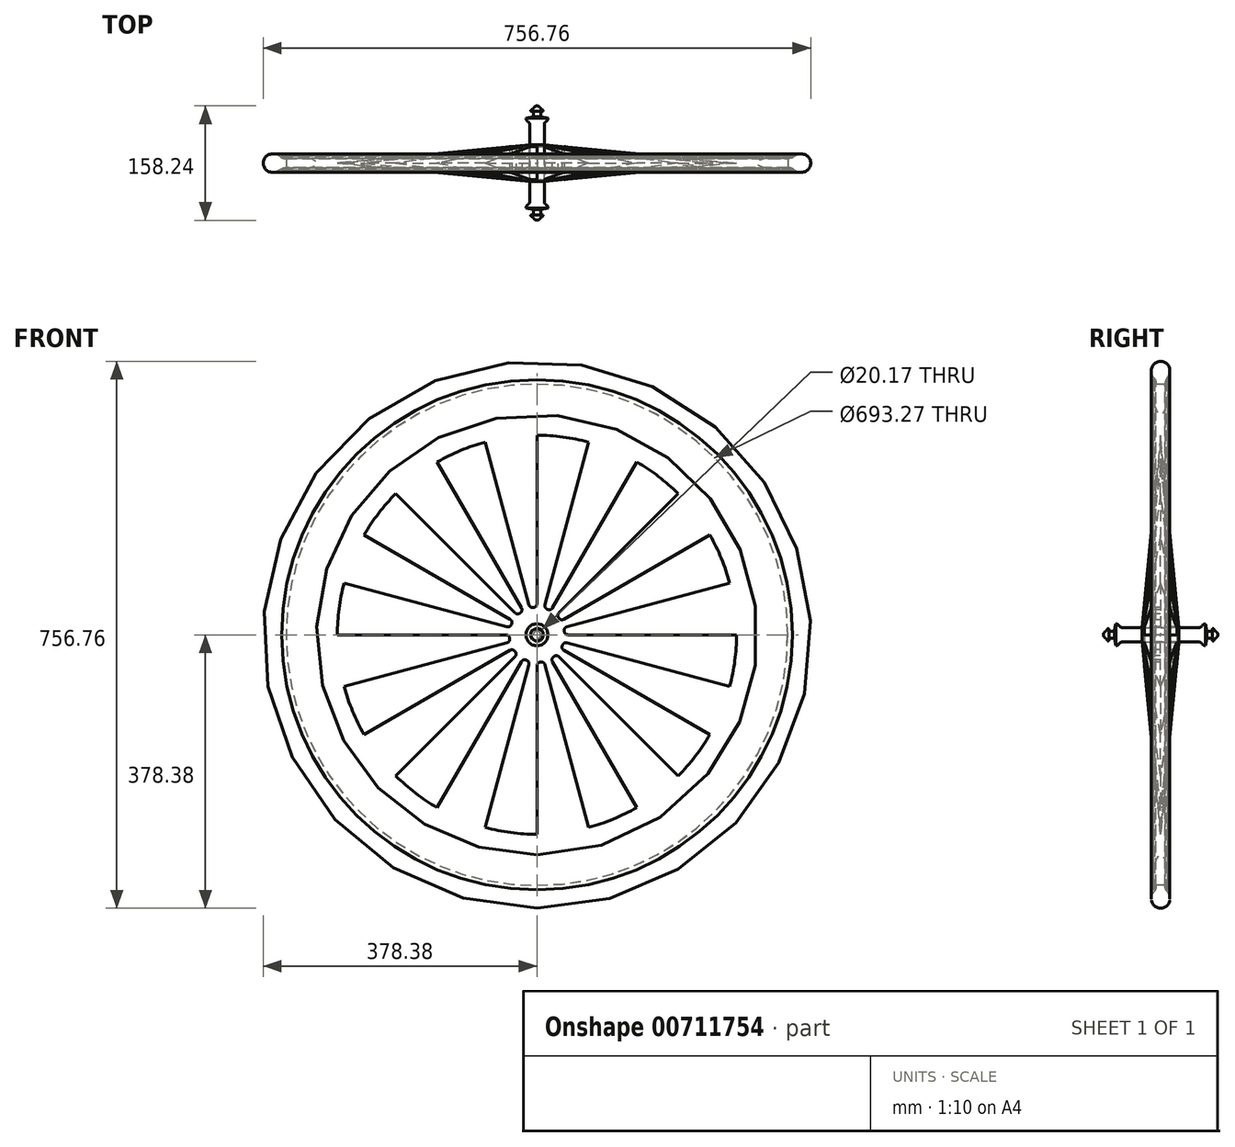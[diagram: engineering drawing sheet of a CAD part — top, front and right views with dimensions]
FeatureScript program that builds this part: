
annotation { "Feature Type Name" : "Feature", "Feature Type Description" : "" }
export const myFeature = defineFeature(function(context is Context, id is Id, definition is map)
    precondition{}
    {
        {
            var Q0;
            Q0=qCreatedBy(makeId("Right.planeOp"),FACE);
            var sketch = newSketch(context, id + "F0", { "sketchPlane" : qUnion([Q0])});
            skLineSegment(sketch, "E0.bottom", {"start": v(71.5, 5) * mm, "end": v(63.88, 5) * mm});
            skPoint(sketch, "E0.middle", {"position": v(0, 0) * mm});
            skLineSegment(sketch, "E1", {"start": v(0, 0) * mm, "end": v(0, 51.2) * mm, "construction": true});
            skLineSegment(sketch, "E2", {"start": v(71.5, 5) * mm, "end": v(71.5, 7.54) * mm});
            skLineSegment(sketch, "E3", {"start": v(71.5, 15) * mm, "end": v(71.5, 19.5) * mm, "construction": true});
            skArc(sketch, "E4", {"start": v(73.4, 8.06) * mm, "mid": v(75.04, 5.82) * mm, "end": v(77.1, 3.96) * mm});
            skArc(sketch, "E5", {"start": v(77.1, 3.96) * mm, "mid": v(78.59, 2.22) * mm, "end": v(79.12, 0) * mm});
            skPoint(sketch, "E6.visualSharp", {"position": v(71.5, 15) * mm});
            skArc(sketch, "E6.filletArc", {"start": v(73.4, 8.06) * mm, "mid": v(72.25, 8.52) * mm, "end": v(71.5, 7.54) * mm});
            skLineSegment(sketch, "E7.MirrorCS", {"start": v(62.09, 15.16) * mm, "end": v(139.74, 15.16) * mm, "construction": true});
            skLineSegment(sketch, "E8.MirrorCS", {"start": v(62.09, 15.16) * mm, "end": v(63.88, 5) * mm});
            skArc(sketch, "E9.MirrorCS", {"start": v(62.09, 15.16) * mm, "mid": v(59.32, 14.42) * mm, "end": v(57.3, 12.38) * mm});
            skArc(sketch, "E10.MirrorCS", {"start": v(53.34, 10.08) * mm, "mid": v(55.62, 10.7) * mm, "end": v(57.3, 12.38) * mm});
            skLineSegment(sketch, "E11.MirrorCS", {"start": v(53.34, 10.08) * mm, "end": v(0, 10.08) * mm});
            skLineSegment(sketch, "E12", {"start": v(0, 0) * mm, "end": v(79.12, 0) * mm});
            skLineSegment(sketch, "E13.MirrorCS", {"start": v(-71.5, 5) * mm, "end": v(-71.5, 7.54) * mm});
            skPoint(sketch, "E14.MirrorP", {"position": v(-71.5, 15) * mm});
            skLineSegment(sketch, "E15.MirrorCS", {"start": v(-71.5, 5) * mm, "end": v(-63.88, 5) * mm});
            skLineSegment(sketch, "E16.MirrorCS", {"start": v(0, 0) * mm, "end": v(-79.12, 0) * mm});
            skArc(sketch, "E17.MirrorCS", {"start": v(-73.4, 8.06) * mm, "mid": v(-75.04, 5.82) * mm, "end": v(-77.1, 3.96) * mm});
            skLineSegment(sketch, "E18.MirrorCS", {"start": v(-71.5, 15) * mm, "end": v(-71.5, 19.5) * mm, "construction": true});
            skLineSegment(sketch, "E19.MirrorCS", {"start": v(-53.34, 10.08) * mm, "end": v(0, 10.08) * mm});
            skLineSegment(sketch, "E20.MirrorCS", {"start": v(-62.09, 15.16) * mm, "end": v(-139.74, 15.16) * mm, "construction": true});
            skArc(sketch, "E21.MirrorCS", {"start": v(-53.34, 10.08) * mm, "mid": v(-55.62, 10.7) * mm, "end": v(-57.3, 12.38) * mm});
            skArc(sketch, "E22.MirrorCS", {"start": v(-62.09, 15.16) * mm, "mid": v(-59.32, 14.42) * mm, "end": v(-57.3, 12.38) * mm});
            skLineSegment(sketch, "E23.MirrorCS", {"start": v(-62.09, 15.16) * mm, "end": v(-63.88, 5) * mm});
            skArc(sketch, "E24.MirrorCS", {"start": v(-73.4, 8.06) * mm, "mid": v(-72.25, 8.52) * mm, "end": v(-71.5, 7.54) * mm});
            skArc(sketch, "E25.MirrorCS", {"start": v(-77.1, 3.96) * mm, "mid": v(-78.59, 2.22) * mm, "end": v(-79.12, 0) * mm});
            skSolve(sketch);
        }
        {
            var Q0;
            Q0=makeQuery(id+"F0.imprint","IMPRINT",FACE,{"disambiguationData":[TD([[makeQuery(id+"F0.imprint","IMPRINT",EDGE,{"derivedFrom":sQuery(id+"F0.wireOp",EDGE,"E0.bottom")}),1.0]])]});
            var Q1;
            Q1=sQuery(id+"F0.wireOp",EDGE,"E16.MirrorCS");
            revolve(context, id + "F1", {"entities" : qUnion([Q0]), "axis" : qUnion([Q1]), "revolveType" : RevolveType.FULL});
        }
        {
            var Q0;
            Q0=qCreatedBy(makeId("Right.planeOp"),FACE);
            var sketch = newSketch(context, id + "F2", { "sketchPlane" : qUnion([Q0])});
            skLineSegment(sketch, "E26", {"start": v(-53.34, 10.08) * mm, "end": v(53.34, 10.08) * mm, "construction": true});
            skArc(sketch, "E27", {"start": v(-57.3, 12.38) * mm, "mid": v(-59.32, 14.42) * mm, "end": v(-62.09, 15.16) * mm, "construction": true});
            skArc(sketch, "E28", {"start": v(-57.3, 12.38) * mm, "mid": v(-55.62, 10.7) * mm, "end": v(-53.34, 10.08) * mm, "construction": true});
            skArc(sketch, "E29", {"start": v(53.34, 10.08) * mm, "mid": v(55.62, 10.7) * mm, "end": v(57.3, 12.38) * mm, "construction": true});
            skArc(sketch, "E30", {"start": v(62.09, 15.16) * mm, "mid": v(59.32, 14.42) * mm, "end": v(57.3, 12.38) * mm, "construction": true});
            skLineSegment(sketch, "E31", {"start": v(0, 10.08) * mm, "end": v(53.34, 10.08) * mm});
            skLineSegment(sketch, "E32", {"start": v(-31.75, 10.08) * mm, "end": v(26.67, 10.08) * mm});
            skLineSegment(sketch, "E33", {"start": v(-53.34, 10.08) * mm, "end": v(0, 365.68) * mm, "construction": true});
            skLineSegment(sketch, "E34", {"start": v(0, 365.68) * mm, "end": v(53.34, 10.08) * mm, "construction": true});
            skArc(sketch, "E35", {"start": v(-1.88, 353.12) * mm, "mid": v(0, 352.98) * mm, "end": v(1.88, 353.12) * mm, "construction": true});
            skLineSegment(sketch, "E36.top", {"start": v(6.35, 346.63) * mm, "end": v(-6.35, 346.63) * mm});
            skPoint(sketch, "E36.middle", {"position": v(0, 352.98) * mm});
            skPoint(sketch, "E37.orphan", {"position": v(-6.35, 359.33) * mm});
            skPoint(sketch, "E38.orphan", {"position": v(6.35, 359.33) * mm});
            skArc(sketch, "E39.trimOffspring", {"start": v(12.6, 367.23) * mm, "mid": v(0, 378.38) * mm, "end": v(-12.6, 367.23) * mm});
            skPoint(sketch, "E40.visualSharp", {"position": v(-6.35, 354.69) * mm});
            skPoint(sketch, "E41.visualSharp", {"position": v(6.35, 354.69) * mm});
            skArc(sketch, "E42", {"start": v(-12.6, 367.23) * mm, "mid": v(-12.07, 360.76) * mm, "end": v(-9, 355.04) * mm});
            skArc(sketch, "E43", {"start": v(-6.35, 346.63) * mm, "mid": v(-6.85, 351.1) * mm, "end": v(-9, 355.04) * mm});
            skArc(sketch, "E44", {"start": v(9, 355.04) * mm, "mid": v(12.07, 360.76) * mm, "end": v(12.6, 367.23) * mm});
            skArc(sketch, "E45", {"start": v(9, 355.04) * mm, "mid": v(6.85, 351.1) * mm, "end": v(6.35, 346.63) * mm});
            skLineSegment(sketch, "E46", {"start": v(0, 365.68) * mm, "end": v(0, 346.63) * mm, "construction": true});
            skArc(sketch, "E47.0", {"start": v(-6.38, 346.6) * mm, "mid": v(-6.56, 349.87) * mm, "end": v(-7.65, 352.96) * mm});
            skLineSegment(sketch, "E47.1", {"start": v(6.38, 346.6) * mm, "end": v(-6.38, 346.6) * mm});
            skArc(sketch, "E47.2", {"start": v(7.65, 352.96) * mm, "mid": v(6.56, 349.87) * mm, "end": v(6.38, 346.6) * mm});
            skLineSegment(sketch, "E48", {"start": v(-7.65, 352.96) * mm, "end": v(-10.16, 352.96) * mm});
            skLineSegment(sketch, "E49", {"start": v(-10.16, 352.96) * mm, "end": v(-10.16, 342.8) * mm});
            skLineSegment(sketch, "E50", {"start": v(-10.16, 342.8) * mm, "end": v(0, 342.8) * mm});
            skLineSegment(sketch, "E51.MirrorCS", {"start": v(10.16, 352.96) * mm, "end": v(10.16, 342.8) * mm});
            skLineSegment(sketch, "E52.MirrorCS", {"start": v(10.16, 342.8) * mm, "end": v(0, 342.8) * mm});
            skLineSegment(sketch, "E53.MirrorCS", {"start": v(7.65, 352.96) * mm, "end": v(10.16, 352.96) * mm});
            skEllipticalArc(sketch, "E54", {});
            skLineSegment(sketch, "E55", {"start": v(0, 342.8) * mm, "end": v(-31.75, 10.08) * mm});
            skLineSegment(sketch, "E56.MirrorCS", {"start": v(0, 342.8) * mm, "end": v(31.75, 10.08) * mm});
            skLineSegment(sketch, "E57.0", {"start": v(0, 275.95) * mm, "end": v(-25.43, 9.48) * mm});
            skLineSegment(sketch, "E57.1", {"start": v(0, 275.95) * mm, "end": v(25.43, 9.48) * mm});
            const initialGuessF2  = {"E54": [0, 0.34279840000000006, 1, 0, 0.01016, 0.0381, 3.141592653589793, 6.283185307179586]};
            skSetInitialGuess(sketch, initialGuessF2);
            skSolve(sketch);
        }
        {
            var Q0;
            Q0=makeQuery(id+"F2.imprint","IMPRINT",FACE,{"disambiguationData":[TD([[makeQuery(id+"F2.imprint","IMPRINT",EDGE,{"derivedFrom":sQuery(id+"F2.wireOp",EDGE,"E36.top")}),-1.0]])]});
            var Q1;
            Q1=makeQuery(id+"F2.imprint","IMPRINT",FACE,{"disambiguationData":[TD([[makeQuery(id+"F2.imprint","IMPRINT",EDGE,{"derivedFrom":sQuery(id+"F2.wireOp",EDGE,"E47.0")}),1.0]])]});
            var Q2;
            {var subQ0=sQuery(id+"F2.wireOp",EDGE,"E50");Q2=makeQuery(id+"F2.imprint","IMPRINT",FACE,{"disambiguationData":[TD([[makeQuery(id+"F2.imprint","IMPRINT",EDGE,{"derivedFrom":subQ0}),-1.0]])]});}
            var Q3;
            {var subQ0=sQuery(id+"F2.wireOp",EDGE,"E52.MirrorCS");Q3=makeQuery(id+"F2.imprint","IMPRINT",FACE,{"disambiguationData":[TD([[makeQuery(id+"F2.imprint","IMPRINT",EDGE,{"derivedFrom":subQ0}),1.0]])]});}
            var Q4;
            {var subQ5=sQuery(id+"F2.wireOp",EDGE,"E32");var subQ7=sQuery(id+"F2.wireOp",EDGE,"E31");var subQ8=makeQuery(id+"F2.imprint","INTERSECT",VERTEX,{"derivedFrom":[subQ7,subQ5]});Q4=makeQuery(id+"F2.imprint","IMPRINT",FACE,{"disambiguationData":[TD([[makeQuery(id+"F2.imprint","IMPRINT",EDGE,{"disambiguationData":[TD([[subQ8,-1.0]])],"derivedFrom":subQ7}),1.0]])]});}
            var Q5;
            {var subQ0=sQuery(id+"F2.wireOp",EDGE,"E55");var subQ1=sQuery(id+"F2.wireOp",EDGE,"E54");var subQ2=makeQuery(id+"F2.imprint","INTERSECT",VERTEX,{"derivedFrom":[subQ1,subQ0]});Q5=makeQuery(id+"F2.imprint","IMPRINT",FACE,{"disambiguationData":[TD([[makeQuery(id+"F2.imprint","IMPRINT",EDGE,{"disambiguationData":[TD([[subQ2,-1.0]])],"derivedFrom":subQ1}),1.0]])]});}
            var Q6;
            Q6=makeQuery(id+"F1.opRevolve","SWEPT_FACE",FACE,{"disambiguationData":[OSD([sQuery(id+"F0.wireOp",EDGE,"E11.MirrorCS"),sQuery(id+"F0.wireOp",EDGE,"E19.MirrorCS")])]});
            revolve(context, id + "F3", {"entities" : qUnion([Q0, Q1, Q2, Q3, Q4, Q5]), "axis" : qUnion([Q6]), "revolveType" : RevolveType.FULL});
        }
        {
            var Q0;
            Q0=qCreatedBy(makeId("Front.planeOp"),FACE);
            var sketch = newSketch(context, id + "F4", { "sketchPlane" : qUnion([Q0])});
            skPoint(sketch, "E58.0", {"position": v(0, 0) * mm});
            skLineSegment(sketch, "E59", {"start": v(0, 42.88) * mm, "end": v(0, 279.11) * mm});
            skLineSegment(sketch, "E60", {"start": v(-11.1, 41.42) * mm, "end": v(-72.24, 269.6) * mm});
            skArc(sketch, "E61", {"start": v(-13.28, 291.8) * mm, "mid": v(-38.13, 289.6) * mm, "end": v(-62.7, 285.3) * mm});
            skArc(sketch, "E62", {"start": v(-4.48, 37.84) * mm, "mid": v(-4.97, 37.77) * mm, "end": v(-5.46, 37.7) * mm});
            skPoint(sketch, "E63.visualSharp", {"position": v(0, 292.1) * mm});
            skArc(sketch, "E63.filletArc", {"start": v(0, 279.11) * mm, "mid": v(-3.93, 288.3) * mm, "end": v(-13.28, 291.8) * mm});
            skPoint(sketch, "E64.visualSharp", {"position": v(-75.6, 282.15) * mm});
            skArc(sketch, "E64.filletArc", {"start": v(-62.7, 285.3) * mm, "mid": v(-70.82, 279.49) * mm, "end": v(-72.24, 269.6) * mm});
            skPoint(sketch, "E65.visualSharp", {"position": v(-9.86, 36.8) * mm});
            skArc(sketch, "E65.filletArc", {"start": v(-11.1, 41.42) * mm, "mid": v(-8.99, 38.5) * mm, "end": v(-5.46, 37.7) * mm});
            skPoint(sketch, "E66.visualSharp", {"position": v(0, 38.1) * mm});
            skArc(sketch, "E66.filletArc", {"start": v(-4.48, 37.84) * mm, "mid": v(-1.28, 39.5) * mm, "end": v(0, 42.88) * mm});
            skLineSegment(sketch, "E67", {"start": v(0, 0) * mm, "end": v(0, 306.93) * mm, "construction": true});
            skLineSegment(sketch, "E68.1.0", {"start": v(0, 0) * mm, "end": v(-153.46, 265.8) * mm, "construction": true});
            skLineSegment(sketch, "E68.1.1", {"start": v(-30.32, 30.32) * mm, "end": v(-197.36, 197.36) * mm});
            skPoint(sketch, "E68.1.2", {"position": v(-19.05, 33) * mm});
            skPoint(sketch, "E68.1.3", {"position": v(-26.94, 26.94) * mm});
            skLineSegment(sketch, "E68.1.4", {"start": v(-21.44, 37.14) * mm, "end": v(-139.56, 241.72) * mm});
            skArc(sketch, "E68.1.5", {"start": v(-22.8, 30.53) * mm, "mid": v(-20.86, 33.57) * mm, "end": v(-21.44, 37.14) * mm});
            skArc(sketch, "E68.1.6", {"start": v(-30.32, 30.32) * mm, "mid": v(-27.03, 28.84) * mm, "end": v(-23.58, 29.92) * mm});
            skArc(sketch, "E68.1.7", {"start": v(-22.8, 30.53) * mm, "mid": v(-23.2, 30.23) * mm, "end": v(-23.58, 29.92) * mm});
            skArc(sketch, "E68.1.8", {"start": v(-196.94, 215.72) * mm, "mid": v(-201.08, 206.63) * mm, "end": v(-197.36, 197.36) * mm});
            skArc(sketch, "E68.1.9", {"start": v(-157.4, 246.07) * mm, "mid": v(-177.82, 231.74) * mm, "end": v(-196.94, 215.72) * mm});
            skArc(sketch, "E68.1.10", {"start": v(-139.56, 241.72) * mm, "mid": v(-147.55, 247.7) * mm, "end": v(-157.4, 246.07) * mm});
            skLineSegment(sketch, "E68.2.0", {"start": v(0, 0) * mm, "end": v(-265.8, 153.46) * mm, "construction": true});
            skLineSegment(sketch, "E68.2.1", {"start": v(-41.42, 11.1) * mm, "end": v(-269.6, 72.24) * mm});
            skPoint(sketch, "E68.2.2", {"position": v(-33, 19.05) * mm});
            skPoint(sketch, "E68.2.3", {"position": v(-36.8, 9.86) * mm});
            skLineSegment(sketch, "E68.2.4", {"start": v(-37.14, 21.44) * mm, "end": v(-241.72, 139.56) * mm});
            skArc(sketch, "E68.2.5", {"start": v(-35, 15.04) * mm, "mid": v(-34.85, 18.64) * mm, "end": v(-37.14, 21.44) * mm});
            skArc(sketch, "E68.2.6", {"start": v(-41.42, 11.1) * mm, "mid": v(-37.83, 11.46) * mm, "end": v(-35.39, 14.12) * mm});
            skArc(sketch, "E68.2.7", {"start": v(-35, 15.04) * mm, "mid": v(-35.2, 14.58) * mm, "end": v(-35.39, 14.12) * mm});
            skArc(sketch, "E68.2.8", {"start": v(-278.42, 88.35) * mm, "mid": v(-277.45, 78.4) * mm, "end": v(-269.6, 72.24) * mm});
            skArc(sketch, "E68.2.9", {"start": v(-259.34, 134.4) * mm, "mid": v(-269.87, 111.78) * mm, "end": v(-278.42, 88.35) * mm});
            skArc(sketch, "E68.2.10", {"start": v(-241.72, 139.56) * mm, "mid": v(-251.63, 140.75) * mm, "end": v(-259.34, 134.4) * mm});
            skLineSegment(sketch, "E68.3.0", {"start": v(0, 0) * mm, "end": v(-306.93, 0) * mm, "construction": true});
            skLineSegment(sketch, "E68.3.1", {"start": v(-41.42, -11.1) * mm, "end": v(-269.6, -72.24) * mm});
            skPoint(sketch, "E68.3.2", {"position": v(-38.1, 0) * mm});
            skPoint(sketch, "E68.3.3", {"position": v(-36.8, -9.86) * mm});
            skLineSegment(sketch, "E68.3.4", {"start": v(-42.88, 0) * mm, "end": v(-279.11, 0) * mm});
            skArc(sketch, "E68.3.5", {"start": v(-37.84, -4.48) * mm, "mid": v(-39.5, -1.28) * mm, "end": v(-42.88, 0) * mm});
            skArc(sketch, "E68.3.6", {"start": v(-41.42, -11.1) * mm, "mid": v(-38.5, -8.99) * mm, "end": v(-37.7, -5.46) * mm});
            skArc(sketch, "E68.3.7", {"start": v(-37.84, -4.48) * mm, "mid": v(-37.77, -4.97) * mm, "end": v(-37.7, -5.46) * mm});
            skArc(sketch, "E68.3.8", {"start": v(-285.3, -62.7) * mm, "mid": v(-279.49, -70.82) * mm, "end": v(-269.6, -72.24) * mm});
            skArc(sketch, "E68.3.9", {"start": v(-291.8, -13.28) * mm, "mid": v(-289.6, -38.13) * mm, "end": v(-285.3, -62.7) * mm});
            skArc(sketch, "E68.3.10", {"start": v(-279.11, 0) * mm, "mid": v(-288.3, -3.93) * mm, "end": v(-291.8, -13.28) * mm});
            skLineSegment(sketch, "E68.4.0", {"start": v(0, 0) * mm, "end": v(-265.8, -153.46) * mm, "construction": true});
            skLineSegment(sketch, "E68.4.1", {"start": v(-30.32, -30.32) * mm, "end": v(-197.36, -197.36) * mm});
            skPoint(sketch, "E68.4.2", {"position": v(-33, -19.05) * mm});
            skPoint(sketch, "E68.4.3", {"position": v(-26.94, -26.94) * mm});
            skLineSegment(sketch, "E68.4.4", {"start": v(-37.14, -21.44) * mm, "end": v(-241.72, -139.56) * mm});
            skArc(sketch, "E68.4.5", {"start": v(-30.53, -22.8) * mm, "mid": v(-33.57, -20.86) * mm, "end": v(-37.14, -21.44) * mm});
            skArc(sketch, "E68.4.6", {"start": v(-30.32, -30.32) * mm, "mid": v(-28.84, -27.03) * mm, "end": v(-29.92, -23.58) * mm});
            skArc(sketch, "E68.4.7", {"start": v(-30.53, -22.8) * mm, "mid": v(-30.23, -23.2) * mm, "end": v(-29.92, -23.58) * mm});
            skArc(sketch, "E68.4.8", {"start": v(-215.72, -196.94) * mm, "mid": v(-206.63, -201.08) * mm, "end": v(-197.36, -197.36) * mm});
            skArc(sketch, "E68.4.9", {"start": v(-246.07, -157.4) * mm, "mid": v(-231.74, -177.82) * mm, "end": v(-215.72, -196.94) * mm});
            skArc(sketch, "E68.4.10", {"start": v(-241.72, -139.56) * mm, "mid": v(-247.7, -147.55) * mm, "end": v(-246.07, -157.4) * mm});
            skLineSegment(sketch, "E68.5.0", {"start": v(0, 0) * mm, "end": v(-153.46, -265.8) * mm, "construction": true});
            skLineSegment(sketch, "E68.5.1", {"start": v(-11.1, -41.42) * mm, "end": v(-72.24, -269.6) * mm});
            skPoint(sketch, "E68.5.2", {"position": v(-19.05, -33) * mm});
            skPoint(sketch, "E68.5.3", {"position": v(-9.86, -36.8) * mm});
            skLineSegment(sketch, "E68.5.4", {"start": v(-21.44, -37.14) * mm, "end": v(-139.56, -241.72) * mm});
            skArc(sketch, "E68.5.5", {"start": v(-15.04, -35) * mm, "mid": v(-18.64, -34.85) * mm, "end": v(-21.44, -37.14) * mm});
            skArc(sketch, "E68.5.6", {"start": v(-11.1, -41.42) * mm, "mid": v(-11.46, -37.83) * mm, "end": v(-14.12, -35.39) * mm});
            skArc(sketch, "E68.5.7", {"start": v(-15.04, -35) * mm, "mid": v(-14.58, -35.2) * mm, "end": v(-14.12, -35.39) * mm});
            skArc(sketch, "E68.5.8", {"start": v(-88.35, -278.42) * mm, "mid": v(-78.4, -277.45) * mm, "end": v(-72.24, -269.6) * mm});
            skArc(sketch, "E68.5.9", {"start": v(-134.4, -259.34) * mm, "mid": v(-111.78, -269.87) * mm, "end": v(-88.35, -278.42) * mm});
            skArc(sketch, "E68.5.10", {"start": v(-139.56, -241.72) * mm, "mid": v(-140.75, -251.63) * mm, "end": v(-134.4, -259.34) * mm});
            skLineSegment(sketch, "E68.6.0", {"start": v(0, 0) * mm, "end": v(0, -306.93) * mm, "construction": true});
            skLineSegment(sketch, "E68.6.1", {"start": v(11.1, -41.42) * mm, "end": v(72.24, -269.6) * mm});
            skPoint(sketch, "E68.6.2", {"position": v(0, -38.1) * mm});
            skPoint(sketch, "E68.6.3", {"position": v(9.86, -36.8) * mm});
            skLineSegment(sketch, "E68.6.4", {"start": v(0, -42.88) * mm, "end": v(0, -279.11) * mm});
            skArc(sketch, "E68.6.5", {"start": v(4.48, -37.84) * mm, "mid": v(1.28, -39.5) * mm, "end": v(0, -42.88) * mm});
            skArc(sketch, "E68.6.6", {"start": v(11.1, -41.42) * mm, "mid": v(8.99, -38.5) * mm, "end": v(5.46, -37.7) * mm});
            skArc(sketch, "E68.6.7", {"start": v(4.48, -37.84) * mm, "mid": v(4.97, -37.77) * mm, "end": v(5.46, -37.7) * mm});
            skArc(sketch, "E68.6.8", {"start": v(62.7, -285.3) * mm, "mid": v(70.82, -279.49) * mm, "end": v(72.24, -269.6) * mm});
            skArc(sketch, "E68.6.9", {"start": v(13.28, -291.8) * mm, "mid": v(38.13, -289.6) * mm, "end": v(62.7, -285.3) * mm});
            skArc(sketch, "E68.6.10", {"start": v(0, -279.11) * mm, "mid": v(3.93, -288.3) * mm, "end": v(13.28, -291.8) * mm});
            skLineSegment(sketch, "E68.7.0", {"start": v(0, 0) * mm, "end": v(153.46, -265.8) * mm, "construction": true});
            skLineSegment(sketch, "E68.7.1", {"start": v(30.32, -30.32) * mm, "end": v(197.36, -197.36) * mm});
            skPoint(sketch, "E68.7.2", {"position": v(19.05, -33) * mm});
            skPoint(sketch, "E68.7.3", {"position": v(26.94, -26.94) * mm});
            skLineSegment(sketch, "E68.7.4", {"start": v(21.44, -37.14) * mm, "end": v(139.56, -241.72) * mm});
            skArc(sketch, "E68.7.5", {"start": v(22.8, -30.53) * mm, "mid": v(20.86, -33.57) * mm, "end": v(21.44, -37.14) * mm});
            skArc(sketch, "E68.7.6", {"start": v(30.32, -30.32) * mm, "mid": v(27.03, -28.84) * mm, "end": v(23.58, -29.92) * mm});
            skArc(sketch, "E68.7.7", {"start": v(22.8, -30.53) * mm, "mid": v(23.2, -30.23) * mm, "end": v(23.58, -29.92) * mm});
            skArc(sketch, "E68.7.8", {"start": v(196.94, -215.72) * mm, "mid": v(201.08, -206.63) * mm, "end": v(197.36, -197.36) * mm});
            skArc(sketch, "E68.7.9", {"start": v(157.4, -246.07) * mm, "mid": v(177.82, -231.74) * mm, "end": v(196.94, -215.72) * mm});
            skArc(sketch, "E68.7.10", {"start": v(139.56, -241.72) * mm, "mid": v(147.55, -247.7) * mm, "end": v(157.4, -246.07) * mm});
            skLineSegment(sketch, "E68.8.0", {"start": v(0, 0) * mm, "end": v(265.8, -153.46) * mm, "construction": true});
            skLineSegment(sketch, "E68.8.1", {"start": v(41.42, -11.1) * mm, "end": v(269.6, -72.24) * mm});
            skPoint(sketch, "E68.8.2", {"position": v(33, -19.05) * mm});
            skPoint(sketch, "E68.8.3", {"position": v(36.8, -9.86) * mm});
            skLineSegment(sketch, "E68.8.4", {"start": v(37.14, -21.44) * mm, "end": v(241.72, -139.56) * mm});
            skArc(sketch, "E68.8.5", {"start": v(35, -15.04) * mm, "mid": v(34.85, -18.64) * mm, "end": v(37.14, -21.44) * mm});
            skArc(sketch, "E68.8.6", {"start": v(41.42, -11.1) * mm, "mid": v(37.83, -11.46) * mm, "end": v(35.39, -14.12) * mm});
            skArc(sketch, "E68.8.7", {"start": v(35, -15.04) * mm, "mid": v(35.2, -14.58) * mm, "end": v(35.39, -14.12) * mm});
            skArc(sketch, "E68.8.8", {"start": v(278.42, -88.35) * mm, "mid": v(277.45, -78.4) * mm, "end": v(269.6, -72.24) * mm});
            skArc(sketch, "E68.8.9", {"start": v(259.34, -134.4) * mm, "mid": v(269.87, -111.78) * mm, "end": v(278.42, -88.35) * mm});
            skArc(sketch, "E68.8.10", {"start": v(241.72, -139.56) * mm, "mid": v(251.63, -140.75) * mm, "end": v(259.34, -134.4) * mm});
            skLineSegment(sketch, "E68.9.0", {"start": v(0, 0) * mm, "end": v(306.93, 0) * mm, "construction": true});
            skLineSegment(sketch, "E68.9.1", {"start": v(41.42, 11.1) * mm, "end": v(269.6, 72.24) * mm});
            skPoint(sketch, "E68.9.2", {"position": v(38.1, 0) * mm});
            skPoint(sketch, "E68.9.3", {"position": v(36.8, 9.86) * mm});
            skLineSegment(sketch, "E68.9.4", {"start": v(42.88, 0) * mm, "end": v(279.11, 0) * mm});
            skArc(sketch, "E68.9.5", {"start": v(37.84, 4.48) * mm, "mid": v(39.5, 1.28) * mm, "end": v(42.88, 0) * mm});
            skArc(sketch, "E68.9.6", {"start": v(41.42, 11.1) * mm, "mid": v(38.5, 8.99) * mm, "end": v(37.7, 5.46) * mm});
            skArc(sketch, "E68.9.7", {"start": v(37.84, 4.48) * mm, "mid": v(37.77, 4.97) * mm, "end": v(37.7, 5.46) * mm});
            skArc(sketch, "E68.9.8", {"start": v(285.3, 62.7) * mm, "mid": v(279.49, 70.82) * mm, "end": v(269.6, 72.24) * mm});
            skArc(sketch, "E68.9.9", {"start": v(291.8, 13.28) * mm, "mid": v(289.6, 38.13) * mm, "end": v(285.3, 62.7) * mm});
            skArc(sketch, "E68.9.10", {"start": v(279.11, 0) * mm, "mid": v(288.3, 3.93) * mm, "end": v(291.8, 13.28) * mm});
            skLineSegment(sketch, "E68.10.0", {"start": v(0, 0) * mm, "end": v(265.8, 153.46) * mm, "construction": true});
            skLineSegment(sketch, "E68.10.1", {"start": v(30.32, 30.32) * mm, "end": v(197.36, 197.36) * mm});
            skPoint(sketch, "E68.10.2", {"position": v(33, 19.05) * mm});
            skPoint(sketch, "E68.10.3", {"position": v(26.94, 26.94) * mm});
            skLineSegment(sketch, "E68.10.4", {"start": v(37.14, 21.44) * mm, "end": v(241.72, 139.56) * mm});
            skArc(sketch, "E68.10.5", {"start": v(30.53, 22.8) * mm, "mid": v(33.57, 20.86) * mm, "end": v(37.14, 21.44) * mm});
            skArc(sketch, "E68.10.6", {"start": v(30.32, 30.32) * mm, "mid": v(28.84, 27.03) * mm, "end": v(29.92, 23.58) * mm});
            skArc(sketch, "E68.10.7", {"start": v(30.53, 22.8) * mm, "mid": v(30.23, 23.2) * mm, "end": v(29.92, 23.58) * mm});
            skArc(sketch, "E68.10.8", {"start": v(215.72, 196.94) * mm, "mid": v(206.63, 201.08) * mm, "end": v(197.36, 197.36) * mm});
            skArc(sketch, "E68.10.9", {"start": v(246.07, 157.4) * mm, "mid": v(231.74, 177.82) * mm, "end": v(215.72, 196.94) * mm});
            skArc(sketch, "E68.10.10", {"start": v(241.72, 139.56) * mm, "mid": v(247.7, 147.55) * mm, "end": v(246.07, 157.4) * mm});
            skLineSegment(sketch, "E68.11.0", {"start": v(0, 0) * mm, "end": v(153.46, 265.8) * mm, "construction": true});
            skLineSegment(sketch, "E68.11.1", {"start": v(11.1, 41.42) * mm, "end": v(72.24, 269.6) * mm});
            skPoint(sketch, "E68.11.2", {"position": v(19.05, 33) * mm});
            skPoint(sketch, "E68.11.3", {"position": v(9.86, 36.8) * mm});
            skLineSegment(sketch, "E68.11.4", {"start": v(21.44, 37.14) * mm, "end": v(139.56, 241.72) * mm});
            skArc(sketch, "E68.11.5", {"start": v(15.04, 35) * mm, "mid": v(18.64, 34.85) * mm, "end": v(21.44, 37.14) * mm});
            skArc(sketch, "E68.11.6", {"start": v(11.1, 41.42) * mm, "mid": v(11.46, 37.83) * mm, "end": v(14.12, 35.39) * mm});
            skArc(sketch, "E68.11.7", {"start": v(15.04, 35) * mm, "mid": v(14.58, 35.2) * mm, "end": v(14.12, 35.39) * mm});
            skArc(sketch, "E68.11.8", {"start": v(88.35, 278.42) * mm, "mid": v(78.4, 277.45) * mm, "end": v(72.24, 269.6) * mm});
            skArc(sketch, "E68.11.9", {"start": v(134.4, 259.34) * mm, "mid": v(111.78, 269.87) * mm, "end": v(88.35, 278.42) * mm});
            skArc(sketch, "E68.11.10", {"start": v(139.56, 241.72) * mm, "mid": v(140.75, 251.63) * mm, "end": v(134.4, 259.34) * mm});
            skSolve(sketch);
        }
        {
            var Q0;
            Q0=qSketchRegion(id+"F4",true);
            extrude(context, id + "F5", {"entities" : qUnion([Q0]), "operationType" : NewBodyOperationType.REMOVE, "endBound" : BoundingType.SYMMETRIC, "oppositeDirection" : true, "depth" : 75.18 * mm, "offsetDistance" : 25.4 * mm});
        }
    });
